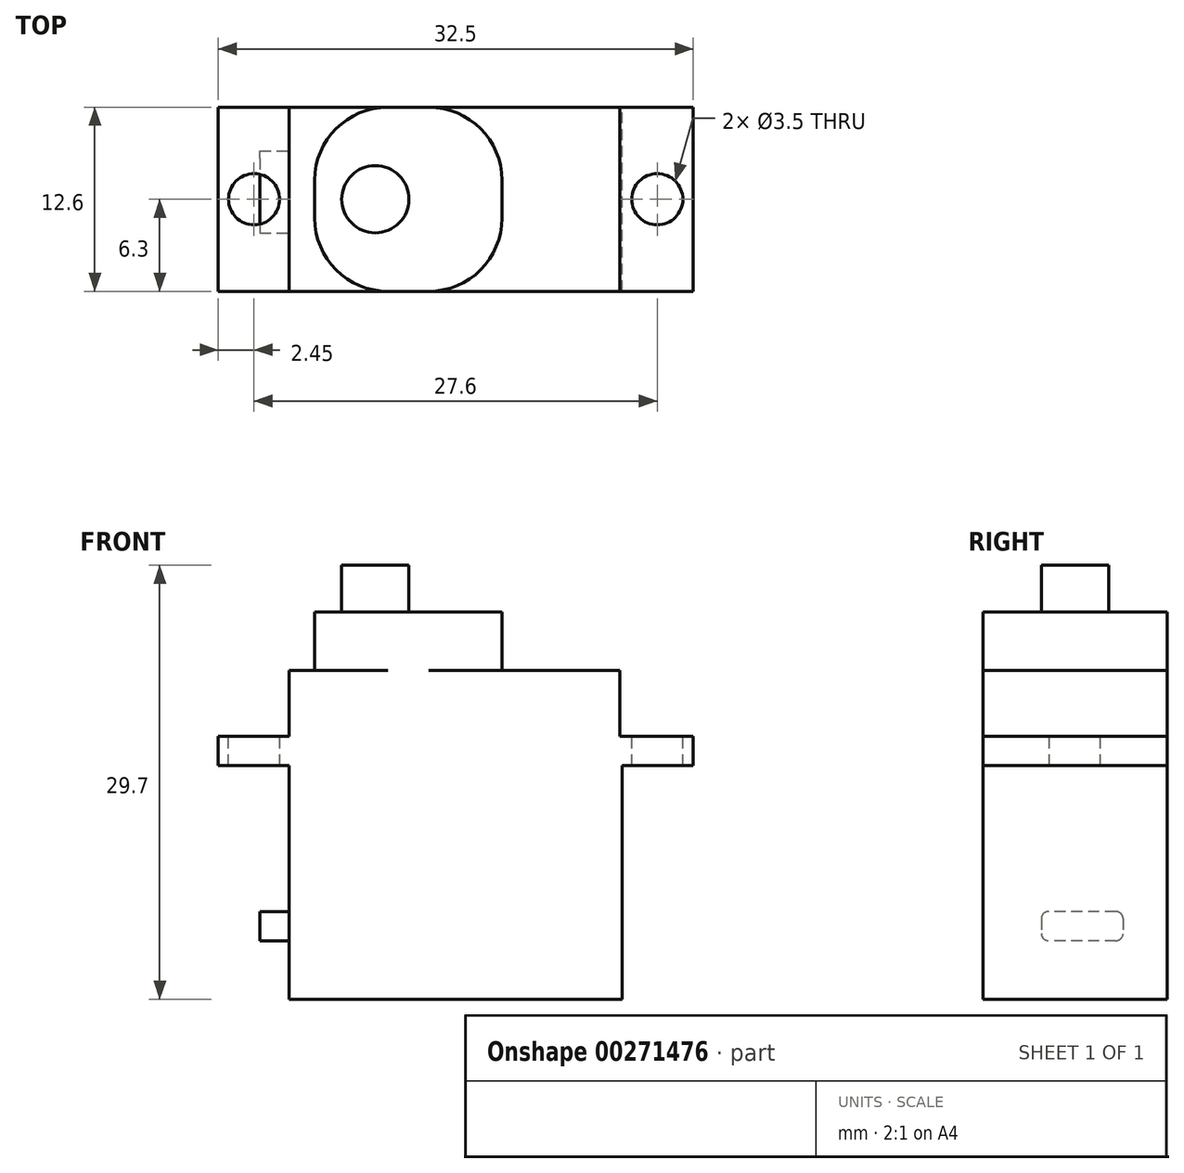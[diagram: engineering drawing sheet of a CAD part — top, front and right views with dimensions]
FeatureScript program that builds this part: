
annotation { "Feature Type Name" : "Feature", "Feature Type Description" : "" }
export const myFeature = defineFeature(function(context is Context, id is Id, definition is map)
    precondition{}
    {
        {
            var Q0;
            Q0=qCreatedBy(makeId("Front.planeOp"),FACE);
            var sketch = newSketch(context, id + "F0", { "sketchPlane" : qUnion([Q0])});
            skLineSegment(sketch, "E0", {"start": v(0, 16) * mm, "end": v(0, 0) * mm});
            skLineSegment(sketch, "E1", {"start": v(0, 0) * mm, "end": v(22.8, 0) * mm});
            skLineSegment(sketch, "E2", {"start": v(22.8, 0) * mm, "end": v(22.8, 16) * mm});
            skLineSegment(sketch, "E3", {"start": v(22.8, 16) * mm, "end": v(27.65, 16) * mm});
            skLineSegment(sketch, "E4", {"start": v(27.65, 16) * mm, "end": v(27.65, 18) * mm});
            skLineSegment(sketch, "E5", {"start": v(27.65, 18) * mm, "end": v(22.65, 18) * mm});
            skLineSegment(sketch, "E6", {"start": v(0, 18) * mm, "end": v(-4.85, 18) * mm});
            skLineSegment(sketch, "E7", {"start": v(-4.85, 18) * mm, "end": v(-4.85, 16) * mm});
            skLineSegment(sketch, "E8", {"start": v(-4.85, 16) * mm, "end": v(0, 16) * mm});
            skLineSegment(sketch, "E9", {"start": v(0, 18) * mm, "end": v(0, 22.5) * mm});
            skLineSegment(sketch, "E10", {"start": v(0, 22.5) * mm, "end": v(1.76, 22.5) * mm});
            skLineSegment(sketch, "E11", {"start": v(1.76, 22.5) * mm, "end": v(1.76, 26.5) * mm});
            skLineSegment(sketch, "E12", {"start": v(1.76, 26.5) * mm, "end": v(14.57, 26.5) * mm});
            skLineSegment(sketch, "E13", {"start": v(14.57, 26.5) * mm, "end": v(14.57, 22.5) * mm});
            skLineSegment(sketch, "E14", {"start": v(14.57, 22.5) * mm, "end": v(22.65, 22.5) * mm});
            skLineSegment(sketch, "E15", {"start": v(22.65, 22.5) * mm, "end": v(22.65, 18) * mm});
            skSolve(sketch);
        }
        {
            var Q0;
            Q0 = qSketchRegion(id + "F0", true);
            extrude(context, id + "F1", {"entities" : qUnion([Q0]), "depth" : 12.6 * mm});
        }
        {
            var Q0;
            Q0=makeQuery(id+"F1.opExtrude","SWEPT_FACE",FACE,{"disambiguationData":[OSD([sQuery(id+"F0.wireOp",EDGE,"E5")])]});
            var sketch = newSketch(context, id + "F2", { "sketchPlane" : qUnion([Q0])});
            skCircle(sketch, "E16", {"center": v(-2.4, -6.3) * mm, "radius": 1.75 * mm});
            skCircle(sketch, "E17", {"center": v(25.2, -6.3) * mm, "radius": 1.75 * mm});
            skLineSegment(sketch, "E18", {"start": v(-4.85, -6.3) * mm, "end": v(-2.4, -6.3) * mm, "construction": true});
            skLineSegment(sketch, "E19", {"start": v(-2.4, -6.3) * mm, "end": v(25.2, -6.3) * mm, "construction": true});
            skLineSegment(sketch, "E20", {"start": v(25.2, -6.3) * mm, "end": v(27.65, -6.3) * mm, "construction": true});
            skSolve(sketch);
        }
        {
            var Q0;
            Q0 = qSketchRegion(id + "F2", true);
            extrude(context, id + "F3", {"entities" : qUnion([Q0]), "operationType" : NewBodyOperationType.REMOVE, "endBound" : BoundingType.UP_TO_NEXT, "oppositeDirection" : true, "depth" : 25 * mm});
        }
        {
            var Q0;
            Q0=makeQuery(id+"F1.opExtrude","SWEPT_FACE",FACE,{"disambiguationData":[OSD([sQuery(id+"F0.wireOp",EDGE,"E12")])]});
            var sketch = newSketch(context, id + "F4", { "sketchPlane" : qUnion([Q0])});
            skCircle(sketch, "E21", {"center": v(5.9, -6.3) * mm, "radius": 2.3 * mm});
            skLineSegment(sketch, "E22", {"start": v(5.9, -6.3) * mm, "end": v(1.76, -6.3) * mm, "construction": true});
            skSolve(sketch);
        }
        {
            var Q0;
            Q0 = qSketchRegion(id + "F4", true);
            extrude(context, id + "F5", {"entities" : qUnion([Q0]), "operationType" : NewBodyOperationType.ADD, "depth" : 3.2 * mm});
        }
        {
            var Q0;
            Q0=makeQuery(id+"F1.opExtrude","CAP_EDGE",EDGE,{"disambiguationData":[OSD([sQuery(id+"F0.wireOp",EDGE,"E13")])],"isStart":true});
            var Q1;
            Q1=makeQuery(id+"F1.opExtrude","CAP_EDGE",EDGE,{"disambiguationData":[OSD([sQuery(id+"F0.wireOp",EDGE,"E13")])],"isStart":false});
            var Q2;
            Q2=makeQuery(id+"F1.opExtrude","CAP_EDGE",EDGE,{"disambiguationData":[OSD([sQuery(id+"F0.wireOp",EDGE,"E11")])],"isStart":false});
            var Q3;
            Q3=makeQuery(id+"F1.opExtrude","CAP_EDGE",EDGE,{"disambiguationData":[OSD([sQuery(id+"F0.wireOp",EDGE,"E11")])],"isStart":true});
            fillet(context, id + "F6", {"entities" : qUnion([Q0, Q1, Q2, Q3]), "radius" : 5 * mm, "tangentPropagation" : true, "allowEdgeOverflow" : false});
        }
        {
            var Q0;
            Q0=makeQuery(id+"F1.opExtrude","SWEPT_FACE",FACE,{"disambiguationData":[OSD([sQuery(id+"F0.wireOp",EDGE,"E0")])]});
            var sketch = newSketch(context, id + "F7", { "sketchPlane" : qUnion([Q0])});
            skLineSegment(sketch, "E23", {"start": v(0, 5) * mm, "end": v(12.6, 5) * mm, "construction": true});
            skLineSegment(sketch, "E24.bottom", {"start": v(3, 6) * mm, "end": v(8.6, 6) * mm});
            skLineSegment(sketch, "E24.top", {"start": v(3, 4) * mm, "end": v(8.6, 4) * mm});
            skLineSegment(sketch, "E24.left", {"start": v(3, 6) * mm, "end": v(3, 4) * mm});
            skLineSegment(sketch, "E24.right", {"start": v(8.6, 6) * mm, "end": v(8.6, 4) * mm});
            skSolve(sketch);
        }
        {
            var Q0;
            Q0=makeQuery(id+"F7.imprint","IMPRINT",FACE,{"disambiguationData":[TD([[makeQuery(id+"F7.imprint","IMPRINT",EDGE,{"derivedFrom":sQuery(id+"F7.wireOp",EDGE,"E24.bottom")}),-1.0]])]});
            extrude(context, id + "F8", {"entities" : qUnion([Q0]), "operationType" : NewBodyOperationType.ADD, "depth" : 2 * mm});
        }
        {
            var Q0;
            Q0=makeQuery(id+"F8.opExtrude","SWEPT_EDGE",EDGE,{"disambiguationData":[OSD([sQuery(id+"F7.wireOp",EDGE,"E24.bottom"),sQuery(id+"F7.wireOp",EDGE,"E24.right")])]});
            var Q1;
            Q1=makeQuery(id+"F8.opExtrude","SWEPT_EDGE",EDGE,{"disambiguationData":[OSD([sQuery(id+"F7.wireOp",EDGE,"E24.bottom"),sQuery(id+"F7.wireOp",EDGE,"E24.left")])]});
            var Q2;
            Q2=makeQuery(id+"F8.opExtrude","SWEPT_EDGE",EDGE,{"disambiguationData":[OSD([sQuery(id+"F7.wireOp",EDGE,"E24.top"),sQuery(id+"F7.wireOp",EDGE,"E24.left")])]});
            var Q3;
            Q3=makeQuery(id+"F8.opExtrude","SWEPT_EDGE",EDGE,{"disambiguationData":[OSD([sQuery(id+"F7.wireOp",EDGE,"E24.top"),sQuery(id+"F7.wireOp",EDGE,"E24.right")])]});
            fillet(context, id + "F9", {"entities" : qUnion([Q0, Q1, Q2, Q3]), "radius" : 0.5 * mm, "tangentPropagation" : true, "allowEdgeOverflow" : false});
        }
    });
